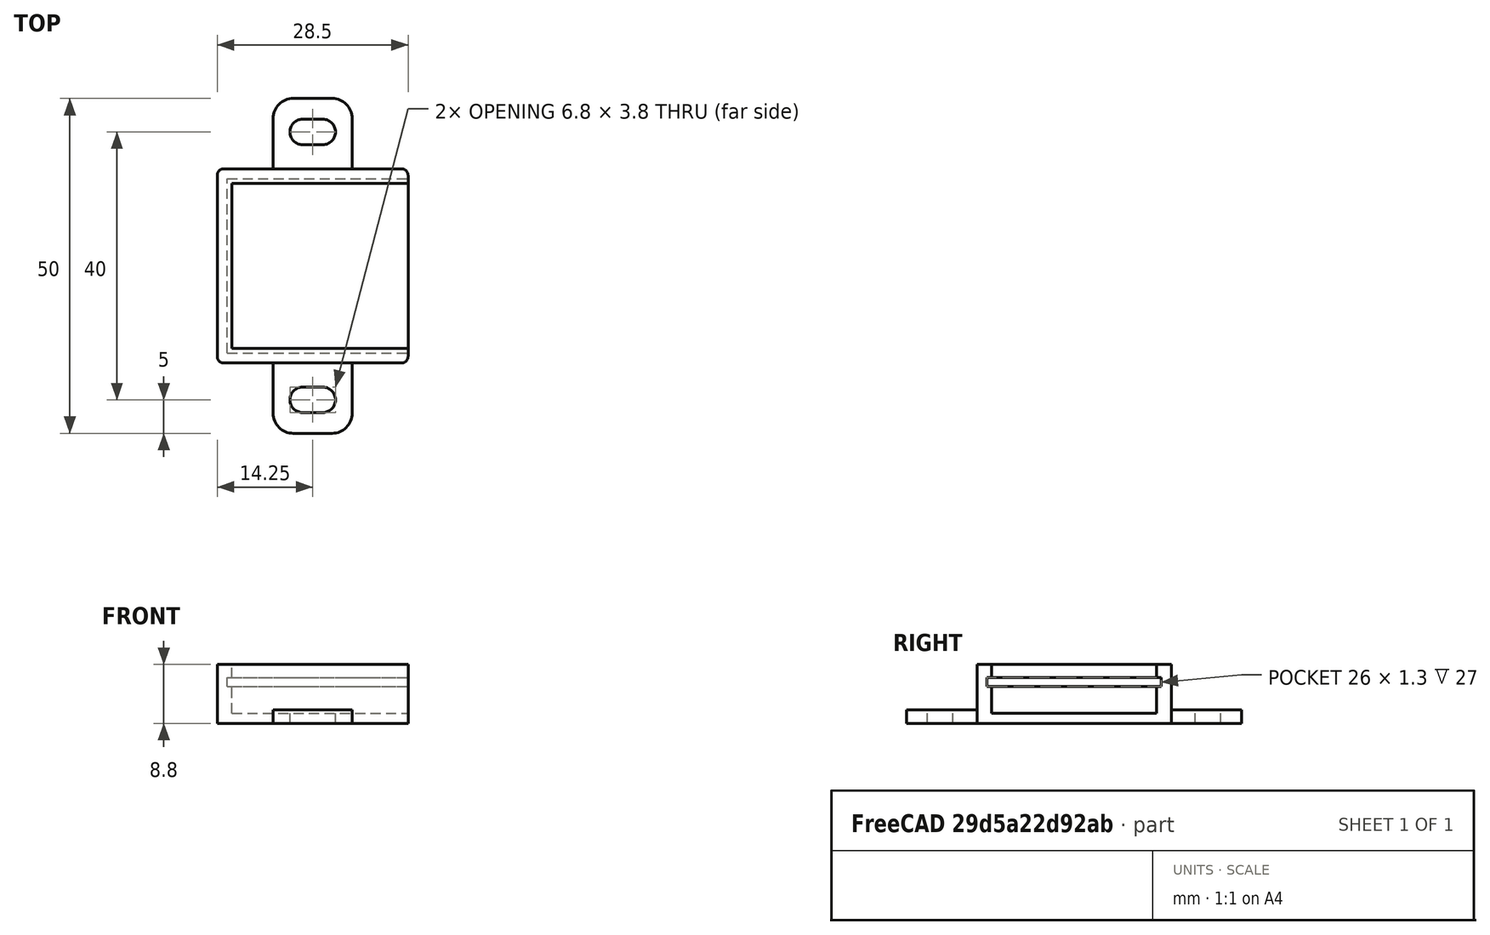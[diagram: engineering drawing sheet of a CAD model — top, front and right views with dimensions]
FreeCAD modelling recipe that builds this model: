
FCSTD DOCUMENT  (FreeCAD 0.19R23578 (Git))
Label: esp8266_d1_mini
License: FreeArt
LicenseURL: http://artlibre.org/licence/lal
objects: Part::Box×3, Part::MultiFuse×2, Spreadsheet::Sheet×1, Part::Fillet×1, Part::Feature×1, Part::Cut×1, App::Part×1
note: 8 computed .brp shape members not serialized (recipe doc carries the construction recipe); baked Part::Feature solids carry a one-line shape summary decoded from their .brp

FEATURE [Spreadsheet::Sheet] Spreadsheet  label="p"
  cells = A1=pcb_x; B1(pcb_x)=27; A2=pcb_y; B2(pcb_y)=26; A3=pcb_z; B3(pcb_z)=1.3; A4=pcb_under; B4(pcb_under)=4; A5=side_wall; B5(side_wall)=1.5; A6=pcb_side_lane; B6(pcb_side_lane)=0.7; A7=bottom_wall; B7(bottom_wall)=1.5; A8=pcb_above; B8(pcb_above)=2
FEATURE [Part::Box] Box  label="external cube"
  AttacherType = Attacher::AttachEngine3D
  Height = 8.8
  Length = 28.5
  Width = 29
  expr: Length = <<p>>.pcb_x + <<p>>.side_wall
  expr: Width = <<p>>.pcb_y + 2 * <<p>>.side_wall
  expr: Height = <<p>>.bottom_wall + <<p>>.pcb_under + <<p>>.pcb_z + <<p>>.pcb_above
FEATURE [Part::Box] Box006  label="internal cube"
  AttacherType = Attacher::AttachEngine3D
  Height = 7.3
  Length = 27.1
  Placement = pos=(2.2,2.2,1.5) rot=(0,0,1;0rad)
  Width = 24.6
  expr: Length = <<p>>.pcb_x - 2 * <<p>>.pcb_side_lane + <<p>>.side_wall
  expr: Width = <<p>>.pcb_y - 2 * <<p>>.pcb_side_lane
  expr: Height = <<p>>.pcb_under + <<p>>.pcb_z + <<p>>.pcb_above
  expr: .Placement.Base.z = <<p>>.bottom_wall
  expr: .Placement.Base.x = <<p>>.side_wall + <<p>>.pcb_side_lane
  expr: .Placement.Base.y = <<p>>.side_wall + <<p>>.pcb_side_lane
FEATURE [Part::Box] Box007  label="pcb extract cube"
  AttacherType = Attacher::AttachEngine3D
  Height = 1.3
  Length = 27
  Placement = pos=(1.5,1.5,5.5) rot=(0,0,1;0rad)
  Width = 26
  expr: Height = <<p>>.pcb_z
  expr: .Placement.Base.z = <<p>>.bottom_wall + <<p>>.pcb_under
  expr: Width = <<p>>.pcb_y
  expr: Length = <<p>>.pcb_x
  expr: .Placement.Base.x = <<p>>.side_wall
  expr: .Placement.Base.y = <<p>>.side_wall
FEATURE [Part::MultiFuse] Fusion  label="extract fusion"
  Shapes = -> [Box006,Box007]
FEATURE [Part::Fillet] Fillet  label="external fillet"
  Base = -> Box
  Edges = 4 edges r=1: [Edge1,Edge3,Edge5,Edge7]
FEATURE [Part::Feature] Cut002001  label="attach plane y dir001"
  Placement = pos=(8.35,-10.5,0) rot=(0,0,1;0rad)
  shape: bbox 11.8 x 50 x 2 mm, 20 faces (baked)
FEATURE [Part::MultiFuse] Fusion001  label="solid fusion"
  Shapes = -> [Fillet,Cut002001]
FEATURE [Part::Cut] Cut  label="body cut"
  Base = -> Fusion001
  Tool = -> Fusion
FEATURE [App::Part] Part  label="esp8266_d1_mini pcb box part"
  Group = -> [Box,Fillet,Fusion001,Fusion,Box007,Box006,Cut]
  Origin = -> Origin
